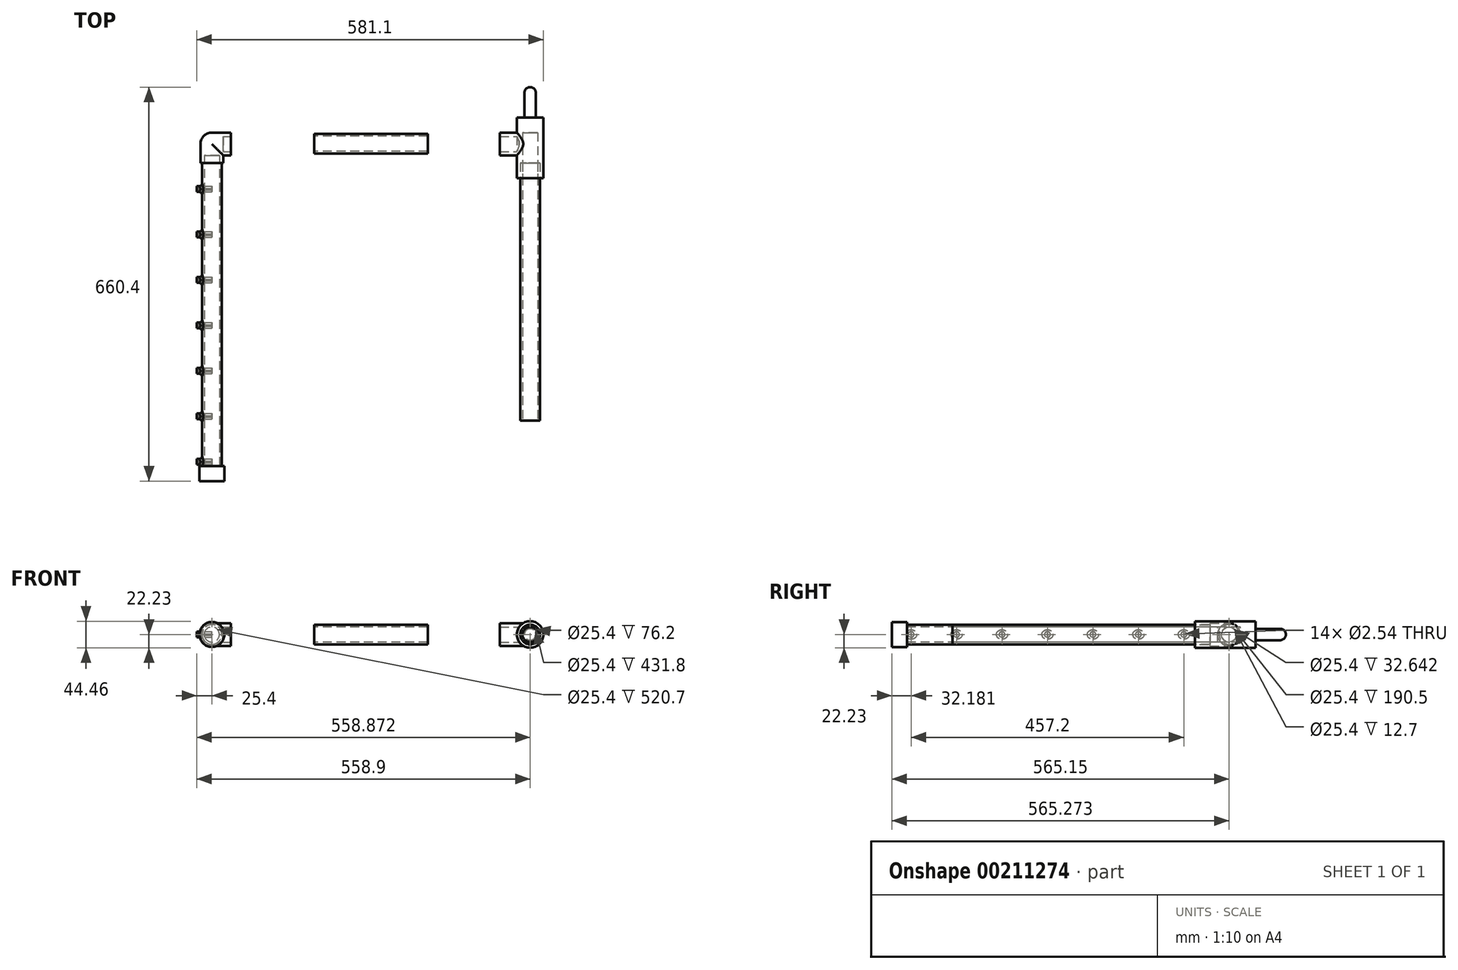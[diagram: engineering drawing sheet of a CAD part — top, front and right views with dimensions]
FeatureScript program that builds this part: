
annotation { "Feature Type Name" : "Feature", "Feature Type Description" : "" }
export const myFeature = defineFeature(function(context is Context, id is Id, definition is map)
    precondition{}
    {
        {
            var Q0;
            Q0=qCreatedBy(makeId("Front.planeOp"),FACE);
            var sketch = newSketch(context, id + "F0", { "sketchPlane" : qUnion([Q0])});
            skLineSegment(sketch, "E0.bottom", {"start": v(19.05, 19.05) * mm, "end": v(-19.05, 19.05) * mm});
            skLineSegment(sketch, "E0.top", {"start": v(19.05, -19.05) * mm, "end": v(-19.05, -19.05) * mm});
            skLineSegment(sketch, "E0.left", {"start": v(19.05, 19.05) * mm, "end": v(19.05, -19.05) * mm});
            skLineSegment(sketch, "E0.right", {"start": v(-19.05, 19.05) * mm, "end": v(-19.05, -19.05) * mm});
            skPoint(sketch, "E0.middle", {"position": v(0, 0) * mm});
            skSolve(sketch);
        }
        {
            var Q0;
            Q0 = qSketchRegion(id + "F0", true);
            extrude(context, id + "F1", {"entities" : qUnion([Q0]), "depth" : 50.8 * mm});
        }
        {
            var Q0;
            Q0=qCreatedBy(makeId("Right.planeOp"),FACE);
            var sketch = newSketch(context, id + "F2", { "sketchPlane" : qUnion([Q0])});
            skLineSegment(sketch, "E1", {"start": v(0, 0) * mm, "end": v(-19.05, 0) * mm});
            skLineSegment(sketch, "E2.bottom", {"start": v(-38.1, 19.05) * mm, "end": v(0, 19.05) * mm});
            skLineSegment(sketch, "E2.top", {"start": v(-38.1, -19.05) * mm, "end": v(0, -19.05) * mm});
            skLineSegment(sketch, "E2.left", {"start": v(-38.1, 19.05) * mm, "end": v(-38.1, -19.05) * mm});
            skLineSegment(sketch, "E2.right", {"start": v(0, 19.05) * mm, "end": v(0, -19.05) * mm});
            skPoint(sketch, "E2.middle", {"position": v(-19.05, 0) * mm});
            skSolve(sketch);
        }
        {
            var Q0;
            Q0 = qSketchRegion(id + "F2", true);
            extrude(context, id + "F3", {"entities" : qUnion([Q0]), "operationType" : NewBodyOperationType.ADD, "depth" : 31.75 * mm});
        }
        {
            var Q0;
            Q0=makeQuery(id+"F1.opExtrude","CAP_EDGE",EDGE,{"disambiguationData":[OSD([sQuery(id+"F0.wireOp",EDGE,"E0.right")])],"isStart":true});
            var Q1;
            Q1=makeQuery(id+"F1.opExtrude","SWEPT_EDGE",EDGE,{"disambiguationData":[OSD([sQuery(id+"F0.wireOp",EDGE,"E0.bottom"),sQuery(id+"F0.wireOp",EDGE,"E0.right")])]});
            var Q2;
            Q2=makeQuery(id+"F3.boolean.opBoolean","MERGE",EDGE,{"derivedFrom":[makeQuery(id+"F1.opExtrude","CAP_EDGE",EDGE,{"disambiguationData":[OSD([sQuery(id+"F0.wireOp",EDGE,"E0.bottom")])],"isStart":true}),makeQuery(id+"F3.opExtrude","SWEPT_EDGE",EDGE,{"disambiguationData":[OSD([sQuery(id+"F2.wireOp",EDGE,"E2.bottom"),sQuery(id+"F2.wireOp",EDGE,"E2.right")])]})]});
            var Q3;
            Q3=makeQuery(id+"F3.boolean.opBoolean","MERGE",EDGE,{"derivedFrom":[makeQuery(id+"F1.opExtrude","CAP_EDGE",EDGE,{"disambiguationData":[OSD([sQuery(id+"F0.wireOp",EDGE,"E0.top")])],"isStart":true}),makeQuery(id+"F3.opExtrude","SWEPT_EDGE",EDGE,{"disambiguationData":[OSD([sQuery(id+"F2.wireOp",EDGE,"E2.top"),sQuery(id+"F2.wireOp",EDGE,"E2.right")])]})]});
            var Q4;
            Q4=makeQuery(id+"F1.opExtrude","SWEPT_EDGE",EDGE,{"disambiguationData":[OSD([sQuery(id+"F0.wireOp",EDGE,"E0.top"),sQuery(id+"F0.wireOp",EDGE,"E0.right")])]});
            var Q5;
            Q5=makeQuery(id+"F3.opExtrude","SWEPT_EDGE",EDGE,{"disambiguationData":[OSD([sQuery(id+"F2.wireOp",EDGE,"E2.top"),sQuery(id+"F2.wireOp",EDGE,"E2.left")])]});
            var Q6;
            Q6=makeQuery(id+"F3.opExtrude","SWEPT_EDGE",EDGE,{"disambiguationData":[OSD([sQuery(id+"F2.wireOp",EDGE,"E2.bottom"),sQuery(id+"F2.wireOp",EDGE,"E2.left")])]});
            var Q7;
            Q7=makeQuery(id+"F1.opExtrude","SWEPT_EDGE",EDGE,{"disambiguationData":[OSD([sQuery(id+"F0.wireOp",EDGE,"E0.bottom"),sQuery(id+"F0.wireOp",EDGE,"E0.left")])]});
            var Q8;
            Q8=makeQuery(id+"F1.opExtrude","SWEPT_EDGE",EDGE,{"disambiguationData":[OSD([sQuery(id+"F0.wireOp",EDGE,"E0.top"),sQuery(id+"F0.wireOp",EDGE,"E0.left")])]});
            fillet(context, id + "F4", {"entities" : qUnion([Q0, Q1, Q2, Q3, Q4, Q5, Q6, Q7, Q8]), "radius" : 19.05 * mm, "tangentPropagation" : true, "allowEdgeOverflow" : false});
        }
        {
            var Q0;
            Q0=makeQuery(id+"F1.opExtrude","CAP_FACE",FACE,{"disambiguationData":[OSD([sQuery(id+"F0.wireOp",EDGE,"E0.bottom"),sQuery(id+"F0.wireOp",EDGE,"E0.top"),sQuery(id+"F0.wireOp",EDGE,"E0.left"),sQuery(id+"F0.wireOp",EDGE,"E0.right")])],"isStart":false});
            var sketch = newSketch(context, id + "F5", { "sketchPlane" : qUnion([Q0])});
            skCircle(sketch, "E3", {"center": v(0, 0) * mm, "radius": 12.7 * mm});
            skSolve(sketch);
        }
        {
            var Q0;
            Q0 = qSketchRegion(id + "F5", true);
            extrude(context, id + "F6", {"entities" : qUnion([Q0]), "operationType" : NewBodyOperationType.REMOVE, "oppositeDirection" : true, "depth" : 12.7 * mm});
        }
        {
            var Q0;
            Q0=makeQuery(id+"F3.opExtrude","CAP_FACE",FACE,{"disambiguationData":[OSD([sQuery(id+"F2.wireOp",EDGE,"E2.bottom"),sQuery(id+"F2.wireOp",EDGE,"E2.top"),sQuery(id+"F2.wireOp",EDGE,"E2.left"),sQuery(id+"F2.wireOp",EDGE,"E2.right")])],"isStart":false});
            var sketch = newSketch(context, id + "F7", { "sketchPlane" : qUnion([Q0])});
            skCircle(sketch, "E4", {"center": v(-19.05, 0) * mm, "radius": 12.7 * mm});
            skSolve(sketch);
        }
        {
            var Q0;
            Q0 = qSketchRegion(id + "F7", true);
            extrude(context, id + "F8", {"entities" : qUnion([Q0]), "operationType" : NewBodyOperationType.REMOVE, "oppositeDirection" : true, "depth" : 12.7 * mm});
        }
        {
            var Q0;
            Q0=qCreatedBy(makeId("Right.planeOp"),FACE);
            cPlane(context, id + "F9", {"entities" : qUnion([Q0]), "cplaneType" : CPlaneType.OFFSET, "offset" : 533.4 * mm, "width" : 152.4 * mm, "height" : 152.4 * mm});
        }
        {
            var Q0;
            Q0=qCreatedBy(id+"F9.planeOp",FACE);
            var sketch = newSketch(context, id + "F10", { "sketchPlane" : qUnion([Q0])});
            skPoint(sketch, "E5", {"position": v(-19.05, 0) * mm});
            skCircle(sketch, "E6", {"center": v(-19.05, 0) * mm, "radius": 19.05 * mm});
            skCircle(sketch, "E7", {"center": v(-19.05, 0) * mm, "radius": 12.7 * mm});
            skSolve(sketch);
        }
        {
            var Q0;
            Q0 = qSketchRegion(id + "F10", true);
            extrude(context, id + "F11", {"entities" : qUnion([Q0]), "oppositeDirection" : true, "depth" : 50.8 * mm});
        }
        {
            var Q0;
            Q0=qCreatedBy(makeId("Front.planeOp"),FACE);
            var sketch = newSketch(context, id + "F12", { "sketchPlane" : qUnion([Q0])});
            skCircle(sketch, "E8", {"center": v(533.47, 0) * mm, "radius": 22.23 * mm});
            skSolve(sketch);
        }
        {
            var Q0;
            Q0 = qSketchRegion(id + "F12", true);
            extrude(context, id + "F13", {"entities" : qUnion([Q0]), "operationType" : NewBodyOperationType.ADD, "endBound" : BoundingType.SYMMETRIC, "depth" : 76.2 * mm});
        }
        {
            var Q0;
            Q0=makeQuery(id+"F13.opExtrude","CAP_FACE",FACE,{"disambiguationData":[OSD([sQuery(id+"F12.wireOp",EDGE,"E8")])],"isStart":false});
            extrude(context, id + "F14", {"entities" : qUnion([Q0]), "operationType" : NewBodyOperationType.ADD, "depth" : 25.4 * mm});
        }
        {
            var Q0;
            Q0=makeQuery(id+"F14.opExtrude","CAP_FACE",FACE,{"disambiguationData":[OSD([sQuery(id+"F12.wireOp",EDGE,"E8")])],"isStart":false});
            var sketch = newSketch(context, id + "F15", { "sketchPlane" : qUnion([Q0])});
            skCircle(sketch, "E9", {"center": v(533.47, 0) * mm, "radius": 9.53 * mm});
            skSolve(sketch);
        }
        {
            var Q0;
            Q0 = qSketchRegion(id + "F15", true);
            extrude(context, id + "F16", {"entities" : qUnion([Q0]), "operationType" : NewBodyOperationType.ADD, "depth" : 50.8 * mm});
        }
        {
            var Q0;
            Q0=makeQuery(id+"F16.opExtrude","CAP_EDGE",EDGE,{"disambiguationData":[OSD([sQuery(id+"F15.wireOp",EDGE,"E9")])],"isStart":false});
            fillet(context, id + "F17", {"entities" : qUnion([Q0]), "radius" : 9.52 * mm, "tangentPropagation" : true, "allowEdgeOverflow" : false});
        }
        {
            var Q0;
            Q0=makeQuery(id+"F13.opExtrude","CAP_FACE",FACE,{"disambiguationData":[OSD([sQuery(id+"F12.wireOp",EDGE,"E8")])],"isStart":true});
            var sketch = newSketch(context, id + "F18", { "sketchPlane" : qUnion([Q0])});
            skCircle(sketch, "E10", {"center": v(-533.47, 0) * mm, "radius": 12.7 * mm});
            skSolve(sketch);
        }
        {
            var Q0;
            Q0 = qSketchRegion(id + "F18", true);
            extrude(context, id + "F19", {"entities" : qUnion([Q0]), "operationType" : NewBodyOperationType.REMOVE, "oppositeDirection" : true, "depth" : 76.2 * mm});
        }
        {
            var Q0;
            Q0=qCreatedBy(makeId("Right.planeOp"),FACE);
            cPlane(context, id + "F20", {"entities" : qUnion([Q0]), "cplaneType" : CPlaneType.OFFSET, "offset" : 266.7 * mm, "width" : 152.4 * mm, "height" : 152.4 * mm});
        }
        {
            var Q0;
            Q0=qCreatedBy(id+"F20.planeOp",FACE);
            var sketch = newSketch(context, id + "F21", { "sketchPlane" : qUnion([Q0])});
            skCircle(sketch, "E11", {"center": v(-18.93, 0) * mm, "radius": 16.51 * mm});
            skCircle(sketch, "E12", {"center": v(-18.93, 0) * mm, "radius": 12.7 * mm});
            skSolve(sketch);
        }
        {
            var Q0;
            Q0 = qSketchRegion(id + "F21", true);
            extrude(context, id + "F22", {"entities" : qUnion([Q0]), "endBound" : BoundingType.SYMMETRIC, "depth" : 190.5 * mm});
        }
        {
            var Q0;
            Q0=makeQuery(id+"F11.opExtrude","SWEPT_BODY",BODY,{"disambiguationData":[OSD([sQuery(id+"F10.wireOp",EDGE,"E6"),sQuery(id+"F10.wireOp",EDGE,"E7")])]});
            var Q1;
            Q1=makeQuery(id+"F11.opExtrude","CAP_EDGE",EDGE,{"disambiguationData":[OSD([sQuery(id+"F10.wireOp",EDGE,"E6")])],"isStart":false});
            transform(context, id + "F23", {"entities" : qUnion([Q0]), "transformType" : TransformType.ROTATION, "transformAxis" : qUnion([Q1]), "angle" : 180 * degree, "makeCopy" : false});
        }
        {
            var Q0;
            Q0=makeQuery(id+"F14.opExtrude","CAP_FACE",FACE,{"disambiguationData":[OSD([sQuery(id+"F12.wireOp",EDGE,"E8")])],"isStart":false});
            cPlane(context, id + "F24", {"entities" : qUnion([Q0]), "cplaneType" : CPlaneType.OFFSET, "offset" : 508 * mm, "oppositeDirection" : true, "width" : 152.4 * mm, "height" : 152.4 * mm});
        }
        {
            var Q0;
            Q0=qCreatedBy(id+"F24.planeOp",FACE);
            var sketch = newSketch(context, id + "F25", { "sketchPlane" : qUnion([Q0])});
            skCircle(sketch, "E13", {"center": v(-533.5, 0) * mm, "radius": 16.51 * mm});
            skCircle(sketch, "E14", {"center": v(-533.5, 0) * mm, "radius": 12.7 * mm});
            skSolve(sketch);
        }
        {
            var Q0;
            Q0 = qSketchRegion(id + "F25", true);
            extrude(context, id + "F26", {"entities" : qUnion([Q0]), "depth" : 431.8 * mm});
        }
        {
            var Q0;
            Q0=qCreatedBy(makeId("Front.planeOp"),FACE);
            cPlane(context, id + "F27", {"entities" : qUnion([Q0]), "cplaneType" : CPlaneType.OFFSET, "offset" : 38.1 * mm, "width" : 152.4 * mm, "height" : 152.4 * mm});
        }
        {
            var Q0;
            Q0=qCreatedBy(id+"F27.planeOp",FACE);
            var sketch = newSketch(context, id + "F28", { "sketchPlane" : qUnion([Q0])});
            skCircle(sketch, "E15", {"center": v(0, 0) * mm, "radius": 16.51 * mm});
            skCircle(sketch, "E16", {"center": v(0, 0) * mm, "radius": 12.7 * mm});
            skSolve(sketch);
        }
        {
            var Q0;
            Q0 = qSketchRegion(id + "F28", true);
            extrude(context, id + "F29", {"entities" : qUnion([Q0]), "operationType" : NewBodyOperationType.ADD, "depth" : 546.1 * mm});
        }
        {
            var Q0;
            Q0=makeQuery(id+"F29.opExtrude","CAP_FACE",FACE,{"disambiguationData":[OSD([sQuery(id+"F28.wireOp",EDGE,"E15"),sQuery(id+"F28.wireOp",EDGE,"E16")])],"isStart":false});
            var sketch = newSketch(context, id + "F30", { "sketchPlane" : qUnion([Q0])});
            skCircle(sketch, "E17", {"center": v(0, 0) * mm, "radius": 20.86 * mm});
            skSolve(sketch);
        }
        {
            var Q0;
            Q0 = qSketchRegion(id + "F30", true);
            extrude(context, id + "F31", {"entities" : qUnion([Q0]), "operationType" : NewBodyOperationType.ADD, "oppositeDirection" : true, "depth" : 25.4 * mm});
        }
        {
            var Q0;
            Q0=qCreatedBy(makeId("Right.planeOp"),FACE);
            var sketch = newSketch(context, id + "F32", { "sketchPlane" : qUnion([Q0])});
            skLineSegment(sketch, "E18", {"start": v(-69.42, 0) * mm, "end": v(-94.82, 0) * mm});
            skLineSegment(sketch, "E19", {"start": v(-94.82, 0) * mm, "end": v(-171.02, 0) * mm});
            skLineSegment(sketch, "E20", {"start": v(-171.02, 0) * mm, "end": v(-247.22, 0) * mm});
            skLineSegment(sketch, "E21", {"start": v(-247.22, 0) * mm, "end": v(-323.42, 0) * mm});
            skLineSegment(sketch, "E22", {"start": v(-323.42, 0) * mm, "end": v(-399.62, 0) * mm});
            skLineSegment(sketch, "E23", {"start": v(-399.62, 0) * mm, "end": v(-475.82, 0) * mm});
            skLineSegment(sketch, "E24", {"start": v(-475.82, 0) * mm, "end": v(-552.02, 0) * mm});
            skCircle(sketch, "E25", {"center": v(-94.82, 0) * mm, "radius": 4.76 * mm});
            skCircle(sketch, "E26", {"center": v(-171.02, 0) * mm, "radius": 4.76 * mm});
            skCircle(sketch, "E27", {"center": v(-247.22, 0) * mm, "radius": 4.76 * mm});
            skCircle(sketch, "E28", {"center": v(-323.42, 0) * mm, "radius": 4.76 * mm});
            skCircle(sketch, "E29", {"center": v(-399.62, 0) * mm, "radius": 4.76 * mm});
            skCircle(sketch, "E30", {"center": v(-475.82, 0) * mm, "radius": 4.76 * mm});
            skCircle(sketch, "E31", {"center": v(-552.02, 0) * mm, "radius": 4.76 * mm});
            skCircle(sketch, "E32", {"center": v(-552.02, 0) * mm, "radius": 1.27 * mm});
            skCircle(sketch, "E33", {"center": v(-475.82, 0) * mm, "radius": 1.27 * mm});
            skCircle(sketch, "E34", {"center": v(-399.62, 0) * mm, "radius": 1.27 * mm});
            skCircle(sketch, "E35", {"center": v(-323.42, 0) * mm, "radius": 1.27 * mm});
            skCircle(sketch, "E36", {"center": v(-247.22, 0) * mm, "radius": 1.27 * mm});
            skCircle(sketch, "E37", {"center": v(-171.02, 0) * mm, "radius": 1.27 * mm});
            skCircle(sketch, "E38", {"center": v(-94.82, 0) * mm, "radius": 1.27 * mm});
            skSolve(sketch);
        }
        {
            var Q0;
            Q0 = qSketchRegion(id + "F32", true);
            extrude(context, id + "F33", {"entities" : qUnion([Q0]), "operationType" : NewBodyOperationType.ADD, "oppositeDirection" : true, "depth" : 25.4 * mm});
        }
        {
            var Q0;
            Q0=makeQuery(id+"F33.boolean.opBoolean","INTERSECT",EDGE,{"derivedFrom":[makeQuery(id+"F29.opExtrude","SWEPT_FACE",FACE,{"disambiguationData":[OSD([sQuery(id+"F28.wireOp",EDGE,"E15")])]}),makeQuery(id+"F33.opExtrude","SWEPT_FACE",FACE,{"disambiguationData":[OSD([sQuery(id+"F32.wireOp",EDGE,"E25")])]})]});
            var Q1;
            Q1=makeQuery(id+"F33.boolean.opBoolean","INTERSECT",EDGE,{"derivedFrom":[makeQuery(id+"F29.opExtrude","SWEPT_FACE",FACE,{"disambiguationData":[OSD([sQuery(id+"F28.wireOp",EDGE,"E15")])]}),makeQuery(id+"F33.opExtrude","SWEPT_FACE",FACE,{"disambiguationData":[OSD([sQuery(id+"F32.wireOp",EDGE,"E26")])]})]});
            var Q2;
            Q2=makeQuery(id+"F33.boolean.opBoolean","INTERSECT",EDGE,{"derivedFrom":[makeQuery(id+"F29.opExtrude","SWEPT_FACE",FACE,{"disambiguationData":[OSD([sQuery(id+"F28.wireOp",EDGE,"E15")])]}),makeQuery(id+"F33.opExtrude","SWEPT_FACE",FACE,{"disambiguationData":[OSD([sQuery(id+"F32.wireOp",EDGE,"E27")])]})]});
            var Q3;
            Q3=makeQuery(id+"F33.boolean.opBoolean","INTERSECT",EDGE,{"derivedFrom":[makeQuery(id+"F29.opExtrude","SWEPT_FACE",FACE,{"disambiguationData":[OSD([sQuery(id+"F28.wireOp",EDGE,"E15")])]}),makeQuery(id+"F33.opExtrude","SWEPT_FACE",FACE,{"disambiguationData":[OSD([sQuery(id+"F32.wireOp",EDGE,"E28")])]})]});
            var Q4;
            Q4=makeQuery(id+"F33.boolean.opBoolean","INTERSECT",EDGE,{"derivedFrom":[makeQuery(id+"F29.opExtrude","SWEPT_FACE",FACE,{"disambiguationData":[OSD([sQuery(id+"F28.wireOp",EDGE,"E15")])]}),makeQuery(id+"F33.opExtrude","SWEPT_FACE",FACE,{"disambiguationData":[OSD([sQuery(id+"F32.wireOp",EDGE,"E29")])]})]});
            var Q5;
            Q5=makeQuery(id+"F33.boolean.opBoolean","INTERSECT",EDGE,{"derivedFrom":[makeQuery(id+"F29.opExtrude","SWEPT_FACE",FACE,{"disambiguationData":[OSD([sQuery(id+"F28.wireOp",EDGE,"E15")])]}),makeQuery(id+"F33.opExtrude","SWEPT_FACE",FACE,{"disambiguationData":[OSD([sQuery(id+"F32.wireOp",EDGE,"E30")])]})]});
            var Q6;
            Q6=makeQuery(id+"F33.boolean.opBoolean","INTERSECT",EDGE,{"derivedFrom":[makeQuery(id+"F29.opExtrude","SWEPT_FACE",FACE,{"disambiguationData":[OSD([sQuery(id+"F28.wireOp",EDGE,"E15")])]}),makeQuery(id+"F33.opExtrude","SWEPT_FACE",FACE,{"disambiguationData":[OSD([sQuery(id+"F32.wireOp",EDGE,"E31")])]})]});
            fillet(context, id + "F34", {"entities" : qUnion([Q0, Q1, Q2, Q3, Q4, Q5, Q6]), "radius" : 5.08 * mm, "tangentPropagation" : true, "allowEdgeOverflow" : false});
        }
    });
